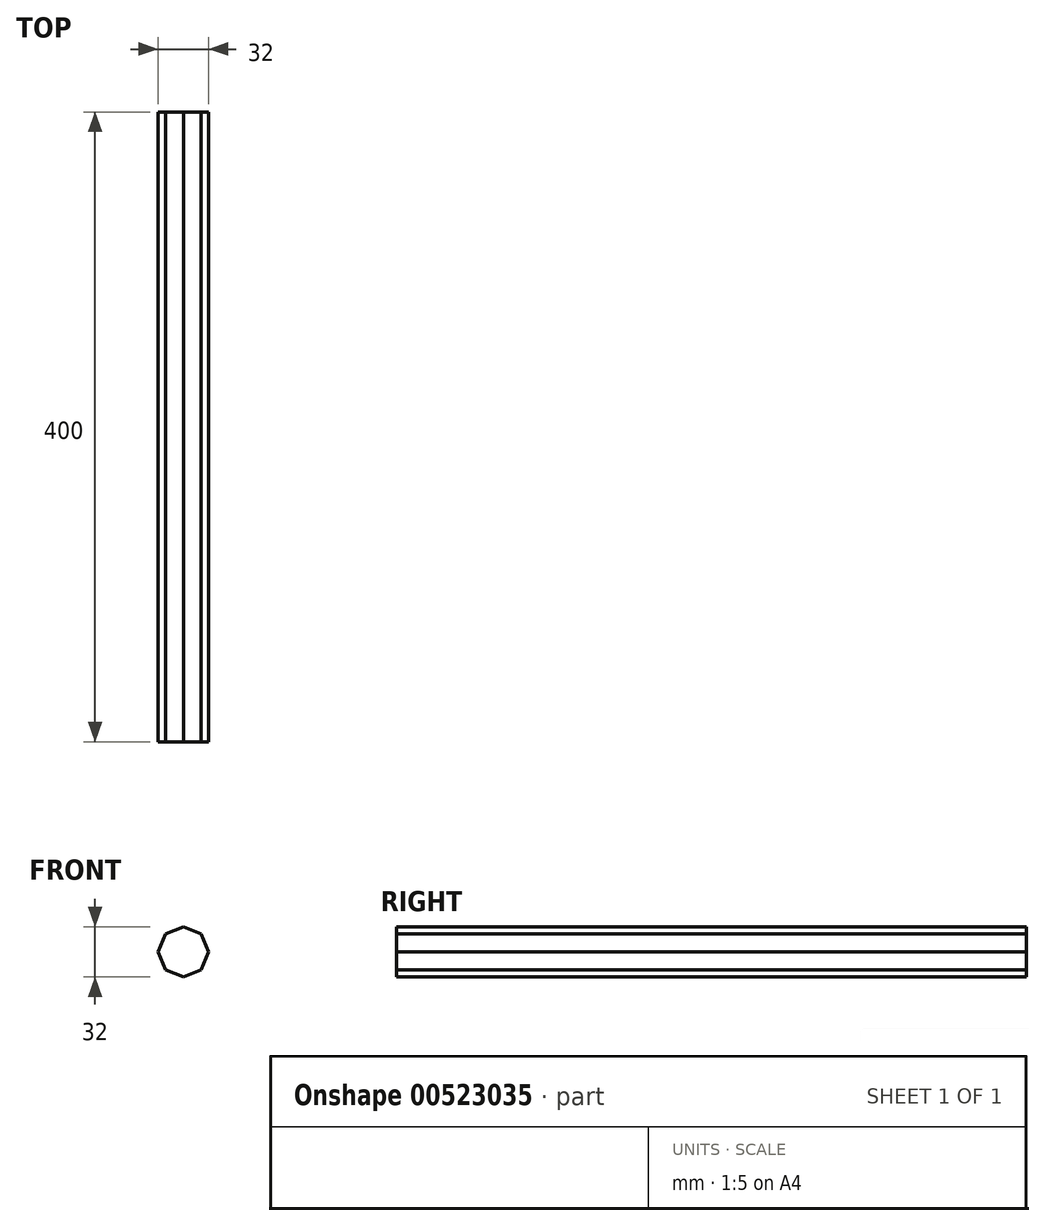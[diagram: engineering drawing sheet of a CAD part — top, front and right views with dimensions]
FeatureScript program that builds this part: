
annotation { "Feature Type Name" : "Feature", "Feature Type Description" : "" }
export const myFeature = defineFeature(function(context is Context, id is Id, definition is map)
    precondition{}
    {
        {
            var Q0;
            Q0=qCreatedBy(makeId("Front.planeOp"),FACE);
            var sketch = newSketch(context, id + "F0", { "sketchPlane" : qUnion([Q0])});
            skCircle(sketch, "E0.cCircle", {"center": v(0, 0) * mm, "radius": 16 * mm, "construction": true});
            skLineSegment(sketch, "E0.0", {"start": v(0, 16) * mm, "end": v(11.31, 11.31) * mm});
            skLineSegment(sketch, "E0.1", {"start": v(11.31, 11.31) * mm, "end": v(16, 0) * mm});
            skLineSegment(sketch, "E0.2", {"start": v(16, 0) * mm, "end": v(11.31, -11.31) * mm});
            skLineSegment(sketch, "E0.3", {"start": v(11.31, -11.31) * mm, "end": v(0, -16) * mm});
            skLineSegment(sketch, "E0.4", {"start": v(0, -16) * mm, "end": v(-11.31, -11.31) * mm});
            skLineSegment(sketch, "E0.5", {"start": v(-11.31, -11.31) * mm, "end": v(-16, 0) * mm});
            skLineSegment(sketch, "E0.6", {"start": v(-16, 0) * mm, "end": v(-11.31, 11.31) * mm});
            skLineSegment(sketch, "E0.7", {"start": v(-11.31, 11.31) * mm, "end": v(0, 16) * mm});
            skLineSegment(sketch, "E1", {"start": v(-16, 0) * mm, "end": v(16, 0) * mm});
            skSolve(sketch);
        }
        {
            var Q0;
            Q0 = qSketchRegion(id + "F0", true);
            extrude(context, id + "F1", {"entities" : qUnion([Q0]), "endBound" : BoundingType.SYMMETRIC, "depth" : 400 * mm, "offsetDistance" : 25 * mm});
        }
    });
